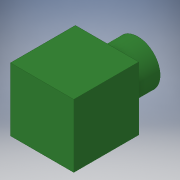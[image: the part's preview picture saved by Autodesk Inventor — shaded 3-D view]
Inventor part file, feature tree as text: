
AUTODESK INVENTOR PART (.ipt)
format: ipt  version: 2019 (Build 230136000, 136)  size: 111,616 bytes
history: native  units: mm
features: extrude x2, sketch x2
ambient origin geometry x8: Origin, YZ Plane, XZ Plane, XY Plane, X Axis, Y Axis, Z Axis, Center Point
bodies: Solid1 (feature_tree)
feature tree (4):
  extrude  "Extrusion1"  Depth=78.0mm
  extrude  "Extrusion2"  Depth=38.0mm
  sketch  "Sketch1"  dims[d0=78.0mm d1=78.0mm]
  sketch  "Sketch2"  dims[d2=80.0mm d3=0.0mm d4=55.0mm d5=47.0mm d6=38.0mm d7=0.0mm]
